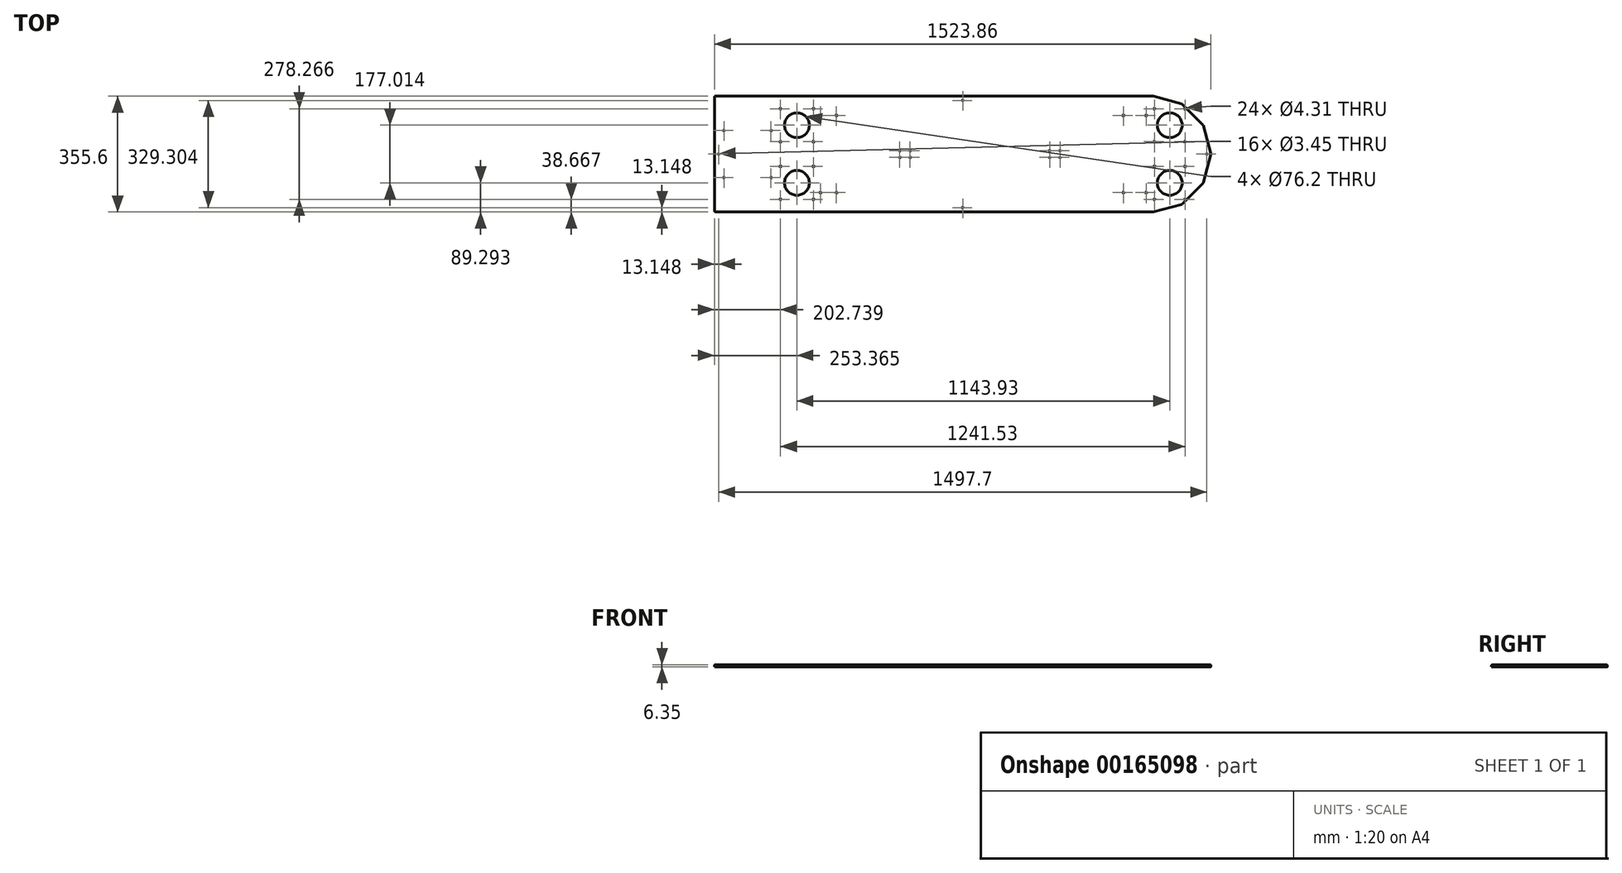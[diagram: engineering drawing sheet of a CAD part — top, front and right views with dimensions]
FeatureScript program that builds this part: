
annotation { "Feature Type Name" : "Feature", "Feature Type Description" : "" }
export const myFeature = defineFeature(function(context is Context, id is Id, definition is map)
    precondition{}
    {
        {
            var Q0;
            Q0=qCreatedBy(makeId("Top.planeOp"),FACE);
            var sketch = newSketch(context, id + "F0", { "sketchPlane" : qUnion([Q0])});
            skLineSegment(sketch, "E0", {"start": v(0, 0) * mm, "end": v(0, -177.8) * mm, "construction": true});
            skLineSegment(sketch, "E1", {"start": v(0, 0) * mm, "end": v(88.9, -153.98) * mm, "construction": true});
            skLineSegment(sketch, "E2", {"start": v(0, 0) * mm, "end": v(153.98, -88.9) * mm, "construction": true});
            skLineSegment(sketch, "E3", {"start": v(0, 0) * mm, "end": v(177.8, 0) * mm, "construction": true});
            skLineSegment(sketch, "E4", {"start": v(0, 0) * mm, "end": v(0, 177.8) * mm, "construction": true});
            skLineSegment(sketch, "E5", {"start": v(0, 0) * mm, "end": v(88.9, 153.98) * mm, "construction": true});
            skLineSegment(sketch, "E6", {"start": v(0, 0) * mm, "end": v(153.98, 88.9) * mm, "construction": true});
            skLineSegment(sketch, "E7", {"start": v(0, 177.8) * mm, "end": v(88.9, 153.98) * mm});
            skLineSegment(sketch, "E8", {"start": v(88.9, 153.98) * mm, "end": v(153.98, 88.9) * mm});
            skLineSegment(sketch, "E9", {"start": v(153.98, 88.9) * mm, "end": v(177.8, 0) * mm});
            skLineSegment(sketch, "E10", {"start": v(177.8, 0) * mm, "end": v(153.98, -88.9) * mm});
            skLineSegment(sketch, "E11", {"start": v(153.98, -88.9) * mm, "end": v(88.9, -153.98) * mm});
            skLineSegment(sketch, "E12", {"start": v(88.9, -153.98) * mm, "end": v(0, -177.8) * mm});
            skLineSegment(sketch, "E13", {"start": v(0, 177.8) * mm, "end": v(-1346.2, 177.8) * mm});
            skLineSegment(sketch, "E14", {"start": v(-1346.2, 177.8) * mm, "end": v(-1346.2, -177.8) * mm});
            skLineSegment(sketch, "E15", {"start": v(-1346.2, -177.8) * mm, "end": v(0, -177.8) * mm});
            skLineSegment(sketch, "E16", {"start": v(-304.8, 0) * mm, "end": v(-304.8, 304.8) * mm, "construction": true});
            skLineSegment(sketch, "E17.bottom", {"start": v(-457.2, 254) * mm, "end": v(-152.4, 254) * mm, "construction": true});
            skLineSegment(sketch, "E17.top", {"start": v(-457.2, 355.6) * mm, "end": v(-152.4, 355.6) * mm, "construction": true});
            skLineSegment(sketch, "E17.left", {"start": v(-457.2, 254) * mm, "end": v(-457.2, 355.6) * mm, "construction": true});
            skLineSegment(sketch, "E17.right", {"start": v(-152.4, 254) * mm, "end": v(-152.4, 355.6) * mm, "construction": true});
            skPoint(sketch, "E17.middle", {"position": v(-304.8, 304.8) * mm});
            skLineSegment(sketch, "E18", {"start": v(0, 0) * mm, "end": v(-304.8, 0) * mm, "construction": true});
            skLineSegment(sketch, "E19", {"start": v(-1346.2, 0) * mm, "end": v(-1244.6, 0) * mm, "construction": true});
            skLineSegment(sketch, "E20.bottom", {"start": v(-1316.83, -72.23) * mm, "end": v(-1172.37, -72.23) * mm, "construction": true});
            skLineSegment(sketch, "E20.top", {"start": v(-1316.83, 72.23) * mm, "end": v(-1172.37, 72.23) * mm, "construction": true});
            skLineSegment(sketch, "E20.left", {"start": v(-1316.83, -72.23) * mm, "end": v(-1316.83, 72.23) * mm, "construction": true});
            skLineSegment(sketch, "E20.right", {"start": v(-1172.37, -72.23) * mm, "end": v(-1172.37, 72.23) * mm, "construction": true});
            skPoint(sketch, "E20.middle", {"position": v(-1244.6, 0) * mm});
            skCircle(sketch, "E21", {"center": v(-1172.37, 72.23) * mm, "radius": 1.73 * mm});
            skCircle(sketch, "E22", {"center": v(-1316.83, 72.23) * mm, "radius": 1.73 * mm});
            skCircle(sketch, "E23", {"center": v(-1316.83, -72.23) * mm, "radius": 1.73 * mm});
            skCircle(sketch, "E24", {"center": v(-1172.37, -72.23) * mm, "radius": 1.73 * mm});
            skSolve(sketch);
        }
        {
            var Q0;
            Q0=makeQuery(id+"F0.imprint","IMPRINT",FACE,{"disambiguationData":[TD([[makeQuery(id+"F0.imprint","IMPRINT",EDGE,{"derivedFrom":sQuery(id+"F0.wireOp",EDGE,"E7")}),-1.0]])]});
            extrude(context, id + "F1", {"entities" : qUnion([Q0]), "depth" : 6.35 * mm});
        }
        {
            var Q0;
            Q0=makeQuery(id+"F1.opExtrude","CAP_FACE",FACE,{"disambiguationData":[OSD([sQuery(id+"F0.wireOp",EDGE,"E7"),sQuery(id+"F0.wireOp",EDGE,"E8"),sQuery(id+"F0.wireOp",EDGE,"E9"),sQuery(id+"F0.wireOp",EDGE,"E10"),sQuery(id+"F0.wireOp",EDGE,"E11"),sQuery(id+"F0.wireOp",EDGE,"E12"),sQuery(id+"F0.wireOp",EDGE,"E13"),sQuery(id+"F0.wireOp",EDGE,"E14"),sQuery(id+"F0.wireOp",EDGE,"E15")])],"isStart":false});
            var sketch = newSketch(context, id + "F2", { "sketchPlane" : qUnion([Q0])});
            skLineSegment(sketch, "E25", {"start": v(164.65, 0) * mm, "end": v(-584.2, 0) * mm, "construction": true});
            skLineSegment(sketch, "E26", {"start": v(-584.2, 0) * mm, "end": v(-1333.05, 0) * mm, "construction": true});
            skLineSegment(sketch, "E27", {"start": v(-1333.05, 0) * mm, "end": v(-1346.2, 0) * mm, "construction": true});
            skLineSegment(sketch, "E28", {"start": v(-584.2, 177.8) * mm, "end": v(-584.2, 164.65) * mm, "construction": true});
            skLineSegment(sketch, "E29", {"start": v(-584.2, 164.65) * mm, "end": v(-584.2, -164.65) * mm, "construction": true});
            skLineSegment(sketch, "E30", {"start": v(-584.2, -164.65) * mm, "end": v(-584.2, -177.8) * mm, "construction": true});
            skCircle(sketch, "E31", {"center": v(-1333.05, 0) * mm, "radius": 1.73 * mm});
            skCircle(sketch, "E32", {"center": v(-584.2, 164.65) * mm, "radius": 1.73 * mm});
            skCircle(sketch, "E33", {"center": v(-584.2, -164.65) * mm, "radius": 1.73 * mm});
            skCircle(sketch, "E34", {"center": v(164.65, 0) * mm, "radius": 1.73 * mm});
            skPoint(sketch, "E35.middle", {"position": v(-584.2, 0) * mm});
            skCircle(sketch, "E36", {"center": v(51.1, 88.5) * mm, "radius": 38.1 * mm});
            skCircle(sketch, "E37", {"center": v(51.1, -88.5) * mm, "radius": 38.1 * mm});
            skCircle(sketch, "E38", {"center": v(-1092.84, 88.5) * mm, "radius": 38.1 * mm});
            skCircle(sketch, "E39", {"center": v(-1092.84, -88.5) * mm, "radius": 38.1 * mm});
            skLineSegment(sketch, "E40.bottom", {"start": v(4.13, 139.13) * mm, "end": v(98.06, 139.13) * mm, "construction": true});
            skLineSegment(sketch, "E40.top", {"start": v(4.13, 37.88) * mm, "end": v(98.06, 37.88) * mm, "construction": true});
            skLineSegment(sketch, "E40.left", {"start": v(4.13, 139.13) * mm, "end": v(4.13, 37.88) * mm, "construction": true});
            skLineSegment(sketch, "E40.right", {"start": v(98.06, 139.13) * mm, "end": v(98.06, 37.88) * mm, "construction": true});
            skLineSegment(sketch, "E41.bottom", {"start": v(4.13, -139.13) * mm, "end": v(98.06, -139.13) * mm, "construction": true});
            skLineSegment(sketch, "E41.top", {"start": v(4.13, -37.88) * mm, "end": v(98.06, -37.88) * mm, "construction": true});
            skLineSegment(sketch, "E41.left", {"start": v(4.13, -139.13) * mm, "end": v(4.13, -37.88) * mm, "construction": true});
            skLineSegment(sketch, "E41.right", {"start": v(98.06, -139.13) * mm, "end": v(98.06, -37.88) * mm, "construction": true});
            skLineSegment(sketch, "E42.bottom", {"start": v(-1143.46, 139.13) * mm, "end": v(-1042.2, 139.13) * mm, "construction": true});
            skLineSegment(sketch, "E42.top", {"start": v(-1143.46, 37.88) * mm, "end": v(-1042.2, 37.88) * mm, "construction": true});
            skLineSegment(sketch, "E42.left", {"start": v(-1143.46, 139.13) * mm, "end": v(-1143.46, 37.88) * mm, "construction": true});
            skLineSegment(sketch, "E42.right", {"start": v(-1042.2, 139.13) * mm, "end": v(-1042.2, 37.88) * mm, "construction": true});
            skLineSegment(sketch, "E43.bottom", {"start": v(-1143.46, -139.13) * mm, "end": v(-1042.2, -139.13) * mm, "construction": true});
            skLineSegment(sketch, "E43.top", {"start": v(-1143.46, -37.88) * mm, "end": v(-1042.2, -37.88) * mm, "construction": true});
            skLineSegment(sketch, "E43.left", {"start": v(-1143.46, -139.13) * mm, "end": v(-1143.46, -37.88) * mm, "construction": true});
            skLineSegment(sketch, "E43.right", {"start": v(-1042.2, -139.13) * mm, "end": v(-1042.2, -37.88) * mm, "construction": true});
            skCircle(sketch, "E44", {"center": v(4.13, -139.13) * mm, "radius": 2.15 * mm});
            skCircle(sketch, "E45", {"center": v(98.06, -139.13) * mm, "radius": 2.15 * mm});
            skCircle(sketch, "E46", {"center": v(98.06, -37.88) * mm, "radius": 2.15 * mm});
            skCircle(sketch, "E47", {"center": v(4.13, -37.88) * mm, "radius": 2.15 * mm});
            skCircle(sketch, "E48", {"center": v(4.13, 37.88) * mm, "radius": 2.15 * mm});
            skCircle(sketch, "E49", {"center": v(4.13, 139.13) * mm, "radius": 2.15 * mm});
            skCircle(sketch, "E50", {"center": v(98.06, 139.13) * mm, "radius": 2.15 * mm});
            skCircle(sketch, "E51", {"center": v(98.06, 139.13) * mm, "radius": 3.97 * mm, "construction": true});
            skCircle(sketch, "E52", {"center": v(-1092.84, 88.5) * mm, "radius": 75.57 * mm, "construction": true});
            skLineSegment(sketch, "E53.bottom", {"start": v(-1316.83, 72.23) * mm, "end": v(-1172.37, 72.23) * mm, "construction": true});
            skLineSegment(sketch, "E53.top", {"start": v(-1316.83, -72.23) * mm, "end": v(-1172.37, -72.23) * mm, "construction": true});
            skLineSegment(sketch, "E53.left", {"start": v(-1316.83, 72.23) * mm, "end": v(-1316.83, -72.23) * mm, "construction": true});
            skLineSegment(sketch, "E53.right", {"start": v(-1172.37, 72.23) * mm, "end": v(-1172.37, -72.23) * mm, "construction": true});
            skPoint(sketch, "E53.middle", {"position": v(-1244.6, 0) * mm});
            skCircle(sketch, "E54", {"center": v(-1172.37, 72.23) * mm, "radius": 3.97 * mm, "construction": true});
            skLineSegment(sketch, "E55", {"start": v(-1168.4, 72.23) * mm, "end": v(-1168.4, 0) * mm, "construction": true});
            skCircle(sketch, "E56", {"center": v(98.06, 37.88) * mm, "radius": 2.15 * mm});
            skCircle(sketch, "E57", {"center": v(-1143.46, -139.13) * mm, "radius": 2.15 * mm});
            skCircle(sketch, "E58", {"center": v(-1042.2, -139.13) * mm, "radius": 2.15 * mm});
            skCircle(sketch, "E59", {"center": v(-1042.2, -37.88) * mm, "radius": 2.15 * mm});
            skCircle(sketch, "E60", {"center": v(-1143.46, -37.88) * mm, "radius": 2.15 * mm});
            skCircle(sketch, "E61", {"center": v(-1143.46, 37.88) * mm, "radius": 2.15 * mm});
            skCircle(sketch, "E62", {"center": v(-1042.2, 37.88) * mm, "radius": 2.15 * mm});
            skCircle(sketch, "E63", {"center": v(-1042.2, 139.13) * mm, "radius": 2.15 * mm});
            skCircle(sketch, "E64", {"center": v(-1143.46, 139.13) * mm, "radius": 2.15 * mm});
            skLineSegment(sketch, "E65.right", {"start": v(-1092.84, 88.5) * mm, "end": v(-1092.84, -88.5) * mm, "construction": true});
            skPoint(sketch, "E66", {"position": v(-1092.83, 0) * mm});
            skLineSegment(sketch, "E67", {"start": v(98.06, -88.5) * mm, "end": v(4.13, -88.5) * mm, "construction": true});
            skLineSegment(sketch, "E68", {"start": v(98.06, 88.5) * mm, "end": v(4.13, 88.5) * mm, "construction": true});
            skCircle(sketch, "E69", {"center": v(164.65, 0) * mm, "radius": 12.7 * mm, "construction": true});
            skCircle(sketch, "E70", {"center": v(51.1, 88.5) * mm, "radius": 73.03 * mm, "construction": true});
            skCircle(sketch, "E71", {"center": v(-1143.46, 139.13) * mm, "radius": 3.97 * mm, "construction": true});
            skLineSegment(sketch, "E72", {"start": v(177.8, 0) * mm, "end": v(177.8, -1701.8) * mm, "construction": true});
            skLineSegment(sketch, "E73", {"start": v(177.8, -1701.8) * mm, "end": v(-1346.2, -1701.8) * mm, "construction": true});
            skLineSegment(sketch, "E74", {"start": v(-1346.2, -1701.8) * mm, "end": v(-1346.2, -177.8) * mm, "construction": true});
            skLineSegment(sketch, "E75", {"start": v(-584.2, -177.8) * mm, "end": v(-584.2, -1701.8) * mm, "construction": true});
            skCircle(sketch, "E76", {"center": v(51.1, -88.5) * mm, "radius": 73.03 * mm, "construction": true});
            skSolve(sketch);
        }
        {
            var Q0;
            Q0=qSketchRegion(id+"F2",true);
            var Q1;
            Q1=makeQuery(id+"F1.opExtrude","CAP_FACE",FACE,{"disambiguationData":[OSD([sQuery(id+"F0.wireOp",EDGE,"E7"),sQuery(id+"F0.wireOp",EDGE,"E8"),sQuery(id+"F0.wireOp",EDGE,"E9"),sQuery(id+"F0.wireOp",EDGE,"E10"),sQuery(id+"F0.wireOp",EDGE,"E11"),sQuery(id+"F0.wireOp",EDGE,"E12"),sQuery(id+"F0.wireOp",EDGE,"E13"),sQuery(id+"F0.wireOp",EDGE,"E14"),sQuery(id+"F0.wireOp",EDGE,"E15")])],"isStart":true});
            extrude(context, id + "F3", {"entities" : qUnion([Q0]), "operationType" : NewBodyOperationType.REMOVE, "endBound" : BoundingType.UP_TO_SURFACE, "oppositeDirection" : true, "endBoundEntityFace" : qUnion([Q1]), "depth" : 25.4 * mm});
        }
        {
            var Q0;
            Q0=makeQuery(id+"F1.opExtrude","CAP_FACE",FACE,{"disambiguationData":[OSD([sQuery(id+"F0.wireOp",EDGE,"E7"),sQuery(id+"F0.wireOp",EDGE,"E8"),sQuery(id+"F0.wireOp",EDGE,"E9"),sQuery(id+"F0.wireOp",EDGE,"E10"),sQuery(id+"F0.wireOp",EDGE,"E11"),sQuery(id+"F0.wireOp",EDGE,"E12"),sQuery(id+"F0.wireOp",EDGE,"E13"),sQuery(id+"F0.wireOp",EDGE,"E14"),sQuery(id+"F0.wireOp",EDGE,"E15")])],"isStart":false});
            var sketch = newSketch(context, id + "F4", { "sketchPlane" : qUnion([Q0])});
            skPoint(sketch, "E77.middle", {"position": v(-531.37, 0) * mm});
            skLineSegment(sketch, "E78", {"start": v(-301.18, 0) * mm, "end": v(-761.56, 0) * mm, "construction": true});
            skLineSegment(sketch, "E79.bottom", {"start": v(-285.3, 10.32) * mm, "end": v(-317.06, 10.32) * mm, "construction": true});
            skLineSegment(sketch, "E79.top", {"start": v(-285.3, -10.32) * mm, "end": v(-317.06, -10.32) * mm, "construction": true});
            skLineSegment(sketch, "E79.left", {"start": v(-285.3, 10.32) * mm, "end": v(-285.3, -10.32) * mm, "construction": true});
            skLineSegment(sketch, "E79.right", {"start": v(-317.06, 10.32) * mm, "end": v(-317.06, -10.32) * mm, "construction": true});
            skPoint(sketch, "E79.middle", {"position": v(-301.18, 0) * mm});
            skLineSegment(sketch, "E80.bottom", {"start": v(-745.68, -10.32) * mm, "end": v(-777.43, -10.32) * mm, "construction": true});
            skLineSegment(sketch, "E80.top", {"start": v(-745.68, 10.32) * mm, "end": v(-777.43, 10.32) * mm, "construction": true});
            skLineSegment(sketch, "E80.left", {"start": v(-745.68, -10.32) * mm, "end": v(-745.68, 10.32) * mm, "construction": true});
            skLineSegment(sketch, "E80.right", {"start": v(-777.43, -10.32) * mm, "end": v(-777.43, 10.32) * mm, "construction": true});
            skPoint(sketch, "E80.middle", {"position": v(-761.56, 0) * mm});
            skCircle(sketch, "E81", {"center": v(-285.3, -10.32) * mm, "radius": 1.73 * mm});
            skCircle(sketch, "E82", {"center": v(-317.06, -10.32) * mm, "radius": 1.73 * mm});
            skCircle(sketch, "E83", {"center": v(-317.06, 10.32) * mm, "radius": 1.73 * mm});
            skCircle(sketch, "E84", {"center": v(-285.3, 10.32) * mm, "radius": 1.73 * mm});
            skCircle(sketch, "E85", {"center": v(-745.68, 10.32) * mm, "radius": 1.73 * mm});
            skCircle(sketch, "E86", {"center": v(-745.68, -10.32) * mm, "radius": 1.73 * mm});
            skCircle(sketch, "E87", {"center": v(-777.43, -10.32) * mm, "radius": 1.73 * mm});
            skCircle(sketch, "E88", {"center": v(-777.43, 10.32) * mm, "radius": 1.73 * mm});
            skLineSegment(sketch, "E89.bottom", {"start": v(-91.03, -118.37) * mm, "end": v(-21.3, -118.37) * mm, "construction": true});
            skLineSegment(sketch, "E89.top", {"start": v(-91.03, 118.37) * mm, "end": v(-21.3, 118.37) * mm, "construction": true});
            skLineSegment(sketch, "E89.left", {"start": v(-91.03, -118.37) * mm, "end": v(-91.03, 118.37) * mm, "construction": true});
            skLineSegment(sketch, "E89.right", {"start": v(-21.3, -118.37) * mm, "end": v(-21.3, 118.37) * mm, "construction": true});
            skPoint(sketch, "E89.middle", {"position": v(-56.16, 0) * mm});
            skCircle(sketch, "E90", {"center": v(-21.3, 118.37) * mm, "radius": 2.15 * mm});
            skCircle(sketch, "E91", {"center": v(-91.03, 118.37) * mm, "radius": 2.15 * mm});
            skCircle(sketch, "E92", {"center": v(-91.03, -118.37) * mm, "radius": 2.15 * mm});
            skCircle(sketch, "E93", {"center": v(-21.3, -118.37) * mm, "radius": 2.15 * mm});
            skLineSegment(sketch, "E94.bottom", {"start": v(-971.7, -118.37) * mm, "end": v(-1020.44, -118.37) * mm, "construction": true});
            skLineSegment(sketch, "E94.top", {"start": v(-971.7, 118.37) * mm, "end": v(-1020.44, 118.37) * mm, "construction": true});
            skLineSegment(sketch, "E94.left", {"start": v(-971.7, -118.37) * mm, "end": v(-971.7, 118.37) * mm, "construction": true});
            skLineSegment(sketch, "E94.right", {"start": v(-1020.44, -118.37) * mm, "end": v(-1020.44, 118.37) * mm, "construction": true});
            skPoint(sketch, "E94.middle", {"position": v(-996.08, 0) * mm});
            skCircle(sketch, "E95", {"center": v(51.1, -88.5) * mm, "radius": 72.4 * mm, "construction": true});
            skCircle(sketch, "E96", {"center": v(-1092.84, -88.5) * mm, "radius": 72.4 * mm, "construction": true});
            skCircle(sketch, "E97", {"center": v(-1020.44, -118.37) * mm, "radius": 2.15 * mm});
            skCircle(sketch, "E98", {"center": v(-971.7, -118.37) * mm, "radius": 2.15 * mm});
            skCircle(sketch, "E99", {"center": v(-1020.44, 118.37) * mm, "radius": 2.15 * mm});
            skCircle(sketch, "E100", {"center": v(-971.7, 118.37) * mm, "radius": 2.15 * mm});
            skLineSegment(sketch, "E101", {"start": v(-971.7, 0) * mm, "end": v(-761.56, 0) * mm, "construction": true});
            skLineSegment(sketch, "E102", {"start": v(-91.03, 0) * mm, "end": v(-301.18, 0) * mm, "construction": true});
            skSolve(sketch);
        }
        {
            var Q0;
            Q0=qSketchRegion(id+"F4",true);
            var Q1;
            Q1=makeQuery(id+"F1.opExtrude","CAP_FACE",FACE,{"disambiguationData":[OSD([sQuery(id+"F0.wireOp",EDGE,"E7"),sQuery(id+"F0.wireOp",EDGE,"E8"),sQuery(id+"F0.wireOp",EDGE,"E9"),sQuery(id+"F0.wireOp",EDGE,"E10"),sQuery(id+"F0.wireOp",EDGE,"E11"),sQuery(id+"F0.wireOp",EDGE,"E12"),sQuery(id+"F0.wireOp",EDGE,"E13"),sQuery(id+"F0.wireOp",EDGE,"E14"),sQuery(id+"F0.wireOp",EDGE,"E15")])],"isStart":true});
            extrude(context, id + "F5", {"entities" : qUnion([Q0]), "operationType" : NewBodyOperationType.REMOVE, "endBound" : BoundingType.UP_TO_SURFACE, "oppositeDirection" : true, "endBoundEntityFace" : qUnion([Q1]), "depth" : 25.4 * mm});
        }
        {
            var Q0;
            Q0=makeQuery(id+"F1.opExtrude","SWEPT_EDGE",EDGE,{"disambiguationData":[OSD([sQuery(id+"F0.wireOp",EDGE,"E12"),sQuery(id+"F0.wireOp",EDGE,"E15")])]});
            var Q1;
            Q1=makeQuery(id+"F1.opExtrude","SWEPT_EDGE",EDGE,{"disambiguationData":[OSD([sQuery(id+"F0.wireOp",EDGE,"E11"),sQuery(id+"F0.wireOp",EDGE,"E12")])]});
            var Q2;
            Q2=makeQuery(id+"F1.opExtrude","SWEPT_EDGE",EDGE,{"disambiguationData":[OSD([sQuery(id+"F0.wireOp",EDGE,"E10"),sQuery(id+"F0.wireOp",EDGE,"E11")])]});
            var Q3;
            Q3=makeQuery(id+"F1.opExtrude","SWEPT_EDGE",EDGE,{"disambiguationData":[OSD([sQuery(id+"F0.wireOp",EDGE,"E9"),sQuery(id+"F0.wireOp",EDGE,"E10")])]});
            var Q4;
            Q4=makeQuery(id+"F1.opExtrude","SWEPT_EDGE",EDGE,{"disambiguationData":[OSD([sQuery(id+"F0.wireOp",EDGE,"E8"),sQuery(id+"F0.wireOp",EDGE,"E9")])]});
            var Q5;
            Q5=makeQuery(id+"F1.opExtrude","SWEPT_EDGE",EDGE,{"disambiguationData":[OSD([sQuery(id+"F0.wireOp",EDGE,"E7"),sQuery(id+"F0.wireOp",EDGE,"E8")])]});
            var Q6;
            Q6=makeQuery(id+"F1.opExtrude","SWEPT_EDGE",EDGE,{"disambiguationData":[OSD([sQuery(id+"F0.wireOp",EDGE,"E7"),sQuery(id+"F0.wireOp",EDGE,"E13")])]});
            var Q7;
            Q7=makeQuery(id+"F1.opExtrude","SWEPT_EDGE",EDGE,{"disambiguationData":[OSD([sQuery(id+"F0.wireOp",EDGE,"E13"),sQuery(id+"F0.wireOp",EDGE,"E14")])]});
            var Q8;
            Q8=makeQuery(id+"F1.opExtrude","SWEPT_EDGE",EDGE,{"disambiguationData":[OSD([sQuery(id+"F0.wireOp",EDGE,"E14"),sQuery(id+"F0.wireOp",EDGE,"E15")])]});
            fillet(context, id + "F6", {"entities" : qUnion([Q0, Q1, Q2, Q3, Q4, Q5, Q6, Q7, Q8]), "radius" : 3.97 * mm, "tangentPropagation" : true, "allowEdgeOverflow" : false});
        }
        {
            var Q0;
            {var subQ0=sQuery(id+"F0.wireOp",EDGE,"E15");var subQ1=sQuery(id+"F0.wireOp",EDGE,"E14");Q0=makeQuery(id+"F6.opFillet","BLEND_EDGE",EDGE,{"blendedFrom":[makeQuery(id+"F1.opExtrude","SWEPT_EDGE",EDGE,{"disambiguationData":[OSD([subQ1,subQ0])]}),makeQuery(id+"F1.opExtrude","CAP_FACE",FACE,{"disambiguationData":[OSD([sQuery(id+"F0.wireOp",EDGE,"E7"),sQuery(id+"F0.wireOp",EDGE,"E8"),sQuery(id+"F0.wireOp",EDGE,"E9"),sQuery(id+"F0.wireOp",EDGE,"E10"),sQuery(id+"F0.wireOp",EDGE,"E11"),sQuery(id+"F0.wireOp",EDGE,"E12"),sQuery(id+"F0.wireOp",EDGE,"E13"),subQ1,subQ0,sQuery(id+"F0.wireOp",EDGE,"E21"),sQuery(id+"F0.wireOp",EDGE,"E22"),sQuery(id+"F0.wireOp",EDGE,"E23"),sQuery(id+"F0.wireOp",EDGE,"E24")])],"isStart":false})],"blendedInto":[makeQuery(id+"F1.opExtrude","CAP_FACE",FACE,{"disambiguationData":[OSD([sQuery(id+"F0.wireOp",EDGE,"E7"),sQuery(id+"F0.wireOp",EDGE,"E8"),sQuery(id+"F0.wireOp",EDGE,"E9"),sQuery(id+"F0.wireOp",EDGE,"E10"),sQuery(id+"F0.wireOp",EDGE,"E11"),sQuery(id+"F0.wireOp",EDGE,"E12"),sQuery(id+"F0.wireOp",EDGE,"E13"),subQ1,subQ0,sQuery(id+"F0.wireOp",EDGE,"E21"),sQuery(id+"F0.wireOp",EDGE,"E22"),sQuery(id+"F0.wireOp",EDGE,"E23"),sQuery(id+"F0.wireOp",EDGE,"E24")])],"isStart":false})]});}
            fillet(context, id + "F7", {"entities" : qUnion([Q0]), "radius" : 3.17 * mm, "tangentPropagation" : true, "allowEdgeOverflow" : false});
        }
    });
